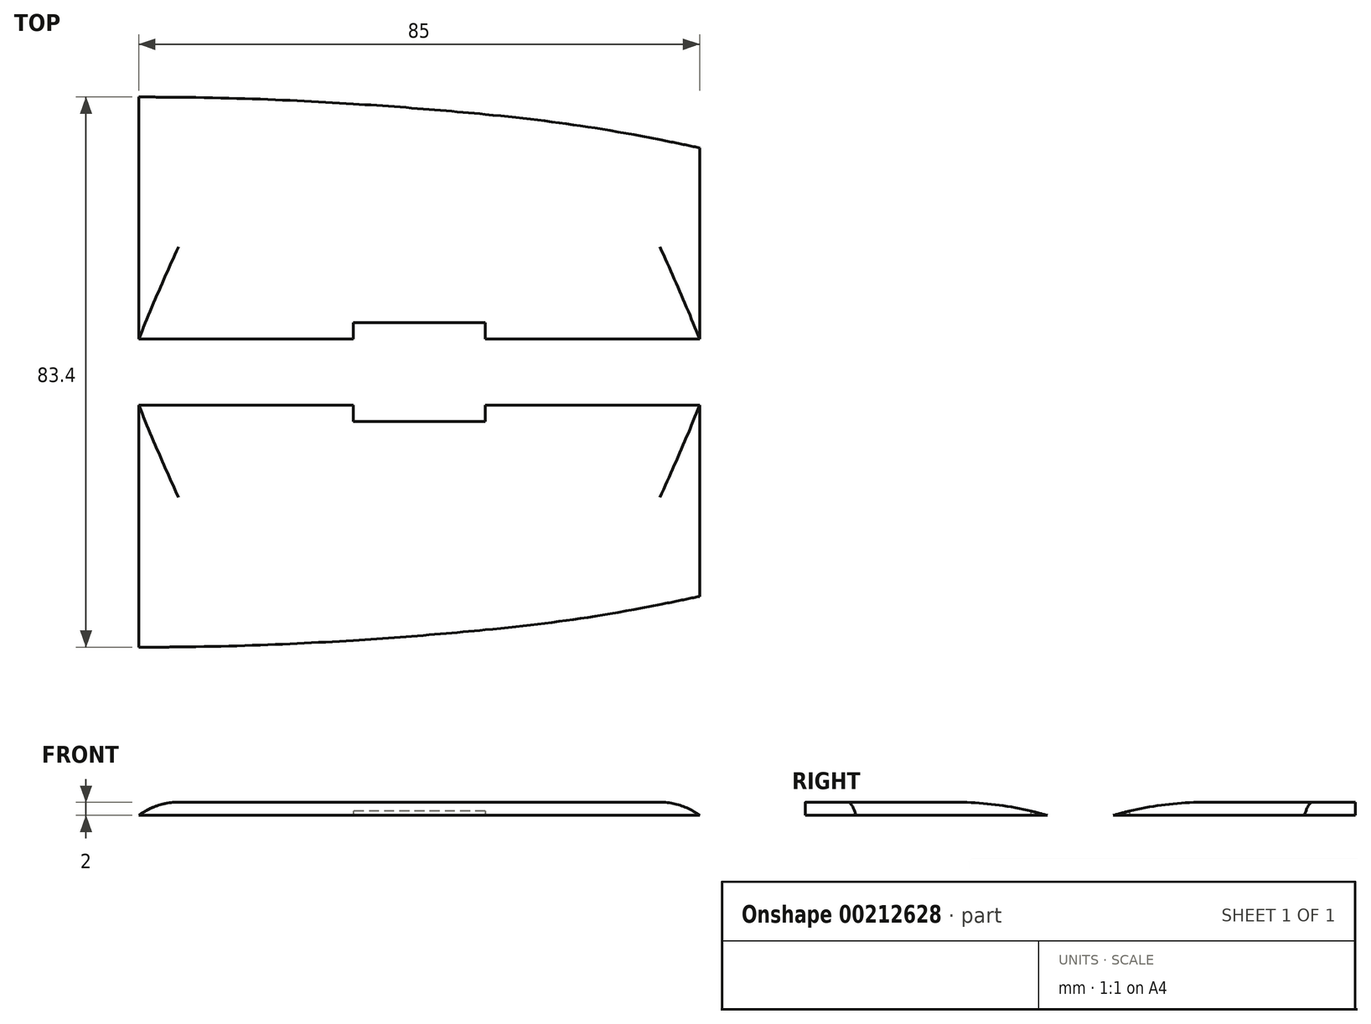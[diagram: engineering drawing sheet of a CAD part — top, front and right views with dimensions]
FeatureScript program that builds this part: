
annotation { "Feature Type Name" : "Feature", "Feature Type Description" : "" }
export const myFeature = defineFeature(function(context is Context, id is Id, definition is map)
    precondition{}
    {
        {
            var Q0;
            Q0=qCreatedBy(makeId("Front.planeOp"),FACE);
            var sketch = newSketch(context, id + "F0", { "sketchPlane" : qUnion([Q0])});
            skLineSegment(sketch, "E0.bottom", {"start": v(0, 0) * mm, "end": v(32.5, 0) * mm});
            skLineSegment(sketch, "E0.left", {"start": v(0, 0) * mm, "end": v(0, 36.7) * mm});
            skLineSegment(sketch, "E0.right", {"start": v(85, 0) * mm, "end": v(85, 29) * mm});
            skPoint(sketch, "E1.start.orphan", {"position": v(42.5, 0) * mm});
            skFitSpline(sketch, "E2", {"points": [v(0, 36.7) * mm, v(34.83, 35.51) * mm, v(59.46, 33.33) * mm, v(85, 29) * mm], "startDerivative": vector(115.5, 0) * mm, "endDerivative": vector(104.16, -22.1) * mm});
            skLineSegment(sketch, "E3", {"start": v(42.5, 0) * mm, "end": v(42.5, 31.95) * mm});
            skPoint(sketch, "E4.orphan", {"position": v(42.5, 57.7) * mm});
            skLineSegment(sketch, "E5.top", {"start": v(32.5, 31.95) * mm, "end": v(52.5, 31.95) * mm});
            skLineSegment(sketch, "E5.left", {"start": v(32.5, 35.67) * mm, "end": v(32.5, 31.95) * mm});
            skLineSegment(sketch, "E5.right", {"start": v(52.5, 34.07) * mm, "end": v(52.5, 31.95) * mm});
            skPoint(sketch, "E6", {"position": v(52.5, 34.07) * mm});
            skPoint(sketch, "E7", {"position": v(32.5, 35.67) * mm});
            skLineSegment(sketch, "E8", {"start": v(-2.73, -19.75) * mm, "end": v(-2.73, 51.35) * mm});
            skLineSegment(sketch, "E9.MirrorCS", {"start": v(-57.96, 34.07) * mm, "end": v(-57.96, 31.95) * mm});
            skLineSegment(sketch, "E10.MirrorCS", {"start": v(-37.96, 31.95) * mm, "end": v(-57.96, 31.95) * mm});
            skLineSegment(sketch, "E11.MirrorCS", {"start": v(-37.96, 35.67) * mm, "end": v(-37.96, 31.95) * mm});
            skFitSpline(sketch, "E12.MirrorCS", {"points": [v(-5.46, 36.7) * mm, v(-40.3, 35.51) * mm, v(-64.92, 33.33) * mm, v(-90.46, 29) * mm], "startDerivative": vector(-115.5, 0) * mm, "endDerivative": vector(-104.16, -22.1) * mm});
            skLineSegment(sketch, "E13.MirrorCS", {"start": v(-90.46, 0) * mm, "end": v(-90.46, 29) * mm});
            skLineSegment(sketch, "E14.MirrorCS", {"start": v(-5.46, 0) * mm, "end": v(-5.46, 36.7) * mm});
            skLineSegment(sketch, "E15.MirrorCS", {"start": v(-5.46, 0) * mm, "end": v(-37.96, 0) * mm});
            skFitSpline(sketch, "E16.MirrorCS", {"points": [v(-5.46, 36.7) * mm, v(-40.3, 35.51) * mm, v(-64.92, 33.33) * mm, v(-90.46, 29) * mm], "startDerivative": vector(-115.5, 0) * mm, "endDerivative": vector(-104.16, -22.1) * mm});
            skLineSegment(sketch, "E17.top", {"start": v(-57.96, 2.5) * mm, "end": v(-37.96, 2.5) * mm});
            skLineSegment(sketch, "E17.left", {"start": v(-57.96, 0) * mm, "end": v(-57.96, 2.5) * mm});
            skLineSegment(sketch, "E17.right", {"start": v(-37.96, 0) * mm, "end": v(-37.96, 2.5) * mm});
            skLineSegment(sketch, "E18.top", {"start": v(32.5, 2.5) * mm, "end": v(52.5, 2.5) * mm});
            skLineSegment(sketch, "E18.left", {"start": v(32.5, 0) * mm, "end": v(32.5, 2.5) * mm});
            skLineSegment(sketch, "E18.right", {"start": v(52.5, 0) * mm, "end": v(52.5, 2.5) * mm});
            skLineSegment(sketch, "E19.trimOffspring", {"start": v(-57.96, 0) * mm, "end": v(-90.46, 0) * mm});
            skLineSegment(sketch, "E20.trimOffspring", {"start": v(52.5, 0) * mm, "end": v(85, 0) * mm});
            skSolve(sketch);
        }
        {
            var Q0;
            Q0 = qSketchRegion(id + "F0", true);
            extrude(context, id + "F1", {"entities" : qUnion([Q0]), "depth" : 2 * mm});
        }
        {
            var Q0;
            Q0=makeQuery(id+"F1.opExtrude","SWEPT_BODY",BODY,{"disambiguationData":[OSD([sQuery(id+"F0.wireOp",EDGE,"E0.bottom"),sQuery(id+"F0.wireOp",EDGE,"E0.left"),sQuery(id+"F0.wireOp",EDGE,"E0.right"),sQuery(id+"F0.wireOp",EDGE,"E2"),sQuery(id+"F0.wireOp",EDGE,"E5.top"),sQuery(id+"F0.wireOp",EDGE,"E5.left"),sQuery(id+"F0.wireOp",EDGE,"E5.right"),sQuery(id+"F0.wireOp",EDGE,"E2"),sQuery(id+"F0.wireOp",EDGE,"E18.top"),sQuery(id+"F0.wireOp",EDGE,"E18.left"),sQuery(id+"F0.wireOp",EDGE,"E18.right"),sQuery(id+"F0.wireOp",EDGE,"E20.trimOffspring")])]});
            var Q1;
            Q1=makeQuery(id+"F1.opExtrude","SWEPT_BODY",BODY,{"disambiguationData":[OSD([sQuery(id+"F0.wireOp",EDGE,"E9.MirrorCS"),sQuery(id+"F0.wireOp",EDGE,"E10.MirrorCS"),sQuery(id+"F0.wireOp",EDGE,"E11.MirrorCS"),sQuery(id+"F0.wireOp",EDGE,"E12.MirrorCS"),sQuery(id+"F0.wireOp",EDGE,"E13.MirrorCS"),sQuery(id+"F0.wireOp",EDGE,"E14.MirrorCS"),sQuery(id+"F0.wireOp",EDGE,"E15.MirrorCS"),sQuery(id+"F0.wireOp",EDGE,"E16.MirrorCS"),sQuery(id+"F0.wireOp",EDGE,"E17.top"),sQuery(id+"F0.wireOp",EDGE,"E17.left"),sQuery(id+"F0.wireOp",EDGE,"E17.right"),sQuery(id+"F0.wireOp",EDGE,"E19.trimOffspring")])]});
            var Q2;
            Q2=makeQuery(id+"F1.opExtrude","CAP_EDGE",EDGE,{"disambiguationData":[OSD([sQuery(id+"F0.wireOp",EDGE,"E0.bottom")])],"isStart":true});
            transform(context, id + "F2", {"entities" : qUnion([Q0, Q1]), "transformType" : TransformType.ROTATION, "transformAxis" : qUnion([Q2]), "angle" : 90 * degree, "oppositeDirection" : true, "makeCopy" : false});
        }
        {
            var Q0;
            Q0=makeQuery(id+"F1.opExtrude","SWEPT_FACE",FACE,{"disambiguationData":[OSD([sQuery(id+"F0.wireOp",EDGE,"E0.bottom")])]});
            cPlane(context, id + "F3", {"entities" : qUnion([Q0]), "cplaneType" : CPlaneType.OFFSET, "offset" : 5 * mm, "width" : 150 * mm, "height" : 150 * mm});
        }
        {
            var Q0;
            Q0=makeQuery(id+"F1.opExtrude","SWEPT_BODY",BODY,{"disambiguationData":[OSD([sQuery(id+"F0.wireOp",EDGE,"E0.bottom"),sQuery(id+"F0.wireOp",EDGE,"E0.left"),sQuery(id+"F0.wireOp",EDGE,"E0.right"),sQuery(id+"F0.wireOp",EDGE,"E2"),sQuery(id+"F0.wireOp",EDGE,"E5.top"),sQuery(id+"F0.wireOp",EDGE,"E5.left"),sQuery(id+"F0.wireOp",EDGE,"E5.right"),sQuery(id+"F0.wireOp",EDGE,"E2"),sQuery(id+"F0.wireOp",EDGE,"E18.top"),sQuery(id+"F0.wireOp",EDGE,"E18.left"),sQuery(id+"F0.wireOp",EDGE,"E18.right"),sQuery(id+"F0.wireOp",EDGE,"E20.trimOffspring")])]});
            var Q1;
            Q1=qCreatedBy(id+"F3.planeOp",FACE);
            mirror(context, id + "F4", {"entities" : qUnion([Q0]), "mirrorPlane" : qUnion([Q1])});
        }
        {
            var Q0;
            Q0=makeQuery(id+"F1.opExtrude","CAP_EDGE",EDGE,{"disambiguationData":[OSD([sQuery(id+"F0.wireOp",EDGE,"E20.trimOffspring")])],"isStart":false});
            fillet(context, id + "F5", {"entities" : qUnion([Q0]), "radius" : 50 * mm, "tangentPropagation" : true, "allowEdgeOverflow" : false});
        }
        {
            var Q0;
            Q0=makeQuery(id+"F4.opPattern","COPY",EDGE,{"derivedFrom":makeQuery(id+"F1.opExtrude","CAP_EDGE",EDGE,{"disambiguationData":[OSD([sQuery(id+"F0.wireOp",EDGE,"E20.trimOffspring")])],"isStart":false}),"instanceName":"1"});
            fillet(context, id + "F6", {"entities" : qUnion([Q0]), "radius" : 50 * mm, "tangentPropagation" : true, "allowEdgeOverflow" : false});
        }
        {
            var Q0;
            Q0=makeQuery(id+"F5.opFillet","BLEND_EDGE",EDGE,{"blendedFrom":[makeQuery(id+"F1.opExtrude","CAP_EDGE",EDGE,{"disambiguationData":[OSD([sQuery(id+"F0.wireOp",EDGE,"E20.trimOffspring")])],"isStart":false}),makeQuery(id+"F1.opExtrude","SWEPT_FACE",FACE,{"disambiguationData":[OSD([sQuery(id+"F0.wireOp",EDGE,"E0.right")])]})],"blendedInto":[makeQuery(id+"F1.opExtrude","SWEPT_FACE",FACE,{"disambiguationData":[OSD([sQuery(id+"F0.wireOp",EDGE,"E0.right")])]})]});
            var Q1;
            Q1=makeQuery(id+"F6.opFillet","BLEND_EDGE",EDGE,{"blendedFrom":[makeQuery(id+"F4.opPattern","COPY",EDGE,{"derivedFrom":makeQuery(id+"F1.opExtrude","CAP_EDGE",EDGE,{"disambiguationData":[OSD([sQuery(id+"F0.wireOp",EDGE,"E20.trimOffspring")])],"isStart":false}),"instanceName":"1"}),makeQuery(id+"F4.opPattern","COPY",FACE,{"derivedFrom":makeQuery(id+"F1.opExtrude","SWEPT_FACE",FACE,{"disambiguationData":[OSD([sQuery(id+"F0.wireOp",EDGE,"E0.right")])]}),"instanceName":"1"})],"blendedInto":[makeQuery(id+"F4.opPattern","COPY",FACE,{"derivedFrom":makeQuery(id+"F1.opExtrude","SWEPT_FACE",FACE,{"disambiguationData":[OSD([sQuery(id+"F0.wireOp",EDGE,"E0.right")])]}),"instanceName":"1"})]});
            var Q2;
            Q2=makeQuery(id+"F1.opExtrude","CAP_EDGE",EDGE,{"disambiguationData":[OSD([sQuery(id+"F0.wireOp",EDGE,"E0.left")])],"isStart":false});
            var Q3;
            Q3=makeQuery(id+"F5.opFillet","BLEND_EDGE",EDGE,{"blendedFrom":[makeQuery(id+"F1.opExtrude","CAP_EDGE",EDGE,{"disambiguationData":[OSD([sQuery(id+"F0.wireOp",EDGE,"E20.trimOffspring")])],"isStart":false}),makeQuery(id+"F1.opExtrude","SWEPT_FACE",FACE,{"disambiguationData":[OSD([sQuery(id+"F0.wireOp",EDGE,"E0.left")])]})],"blendedInto":[makeQuery(id+"F1.opExtrude","SWEPT_FACE",FACE,{"disambiguationData":[OSD([sQuery(id+"F0.wireOp",EDGE,"E0.left")])]})]});
            var Q4;
            Q4=makeQuery(id+"F6.opFillet","BLEND_EDGE",EDGE,{"blendedFrom":[makeQuery(id+"F4.opPattern","COPY",EDGE,{"derivedFrom":makeQuery(id+"F1.opExtrude","CAP_EDGE",EDGE,{"disambiguationData":[OSD([sQuery(id+"F0.wireOp",EDGE,"E20.trimOffspring")])],"isStart":false}),"instanceName":"1"}),makeQuery(id+"F4.opPattern","COPY",FACE,{"derivedFrom":makeQuery(id+"F1.opExtrude","SWEPT_FACE",FACE,{"disambiguationData":[OSD([sQuery(id+"F0.wireOp",EDGE,"E0.left")])]}),"instanceName":"1"})],"blendedInto":[makeQuery(id+"F4.opPattern","COPY",FACE,{"derivedFrom":makeQuery(id+"F1.opExtrude","SWEPT_FACE",FACE,{"disambiguationData":[OSD([sQuery(id+"F0.wireOp",EDGE,"E0.left")])]}),"instanceName":"1"})]});
            var Q5;
            Q5=makeQuery(id+"F4.opPattern","COPY",EDGE,{"derivedFrom":makeQuery(id+"F1.opExtrude","CAP_EDGE",EDGE,{"disambiguationData":[OSD([sQuery(id+"F0.wireOp",EDGE,"E0.left")])],"isStart":false}),"instanceName":"1"});
            fillet(context, id + "F7", {"entities" : qUnion([Q0, Q1, Q2, Q3, Q4, Q5]), "radius" : 10 * mm, "tangentPropagation" : true, "allowEdgeOverflow" : false});
        }
        {
            var Q0;
            Q0=makeQuery(id+"F1.opExtrude","SWEPT_BODY",BODY,{"disambiguationData":[OSD([sQuery(id+"F0.wireOp",EDGE,"E9.MirrorCS"),sQuery(id+"F0.wireOp",EDGE,"E10.MirrorCS"),sQuery(id+"F0.wireOp",EDGE,"E11.MirrorCS"),sQuery(id+"F0.wireOp",EDGE,"E12.MirrorCS"),sQuery(id+"F0.wireOp",EDGE,"E13.MirrorCS"),sQuery(id+"F0.wireOp",EDGE,"E14.MirrorCS"),sQuery(id+"F0.wireOp",EDGE,"E15.MirrorCS"),sQuery(id+"F0.wireOp",EDGE,"E16.MirrorCS"),sQuery(id+"F0.wireOp",EDGE,"E17.top"),sQuery(id+"F0.wireOp",EDGE,"E17.left"),sQuery(id+"F0.wireOp",EDGE,"E17.right"),sQuery(id+"F0.wireOp",EDGE,"E19.trimOffspring")])]});
            deleteBodies(context, id + "F8", {"entities" : qUnion([Q0])});
        }
    });
